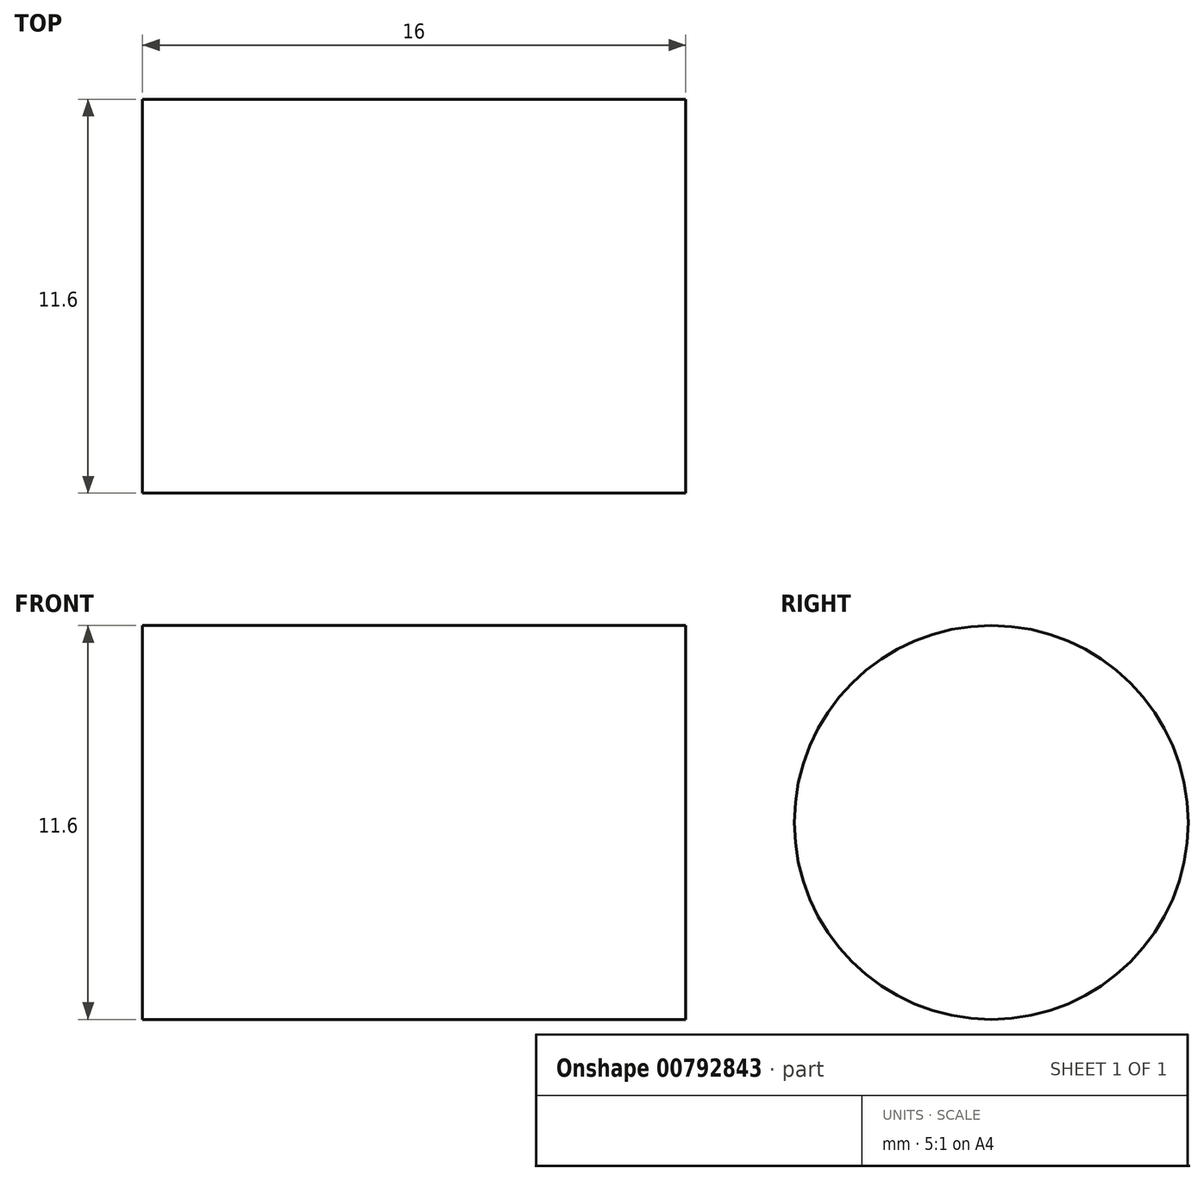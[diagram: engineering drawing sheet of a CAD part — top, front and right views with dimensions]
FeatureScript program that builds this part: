
annotation { "Feature Type Name" : "Feature", "Feature Type Description" : "" }
export const myFeature = defineFeature(function(context is Context, id is Id, definition is map)
    precondition{}
    {
        {
            var Q0;
            Q0=qCreatedBy(makeId("Right.planeOp"), FACE);
            var sketch = newSketch(context, id + "F0", { "sketchPlane" : qUnion([Q0])});
            skCircle(sketch, "E0", {"center": v(0, 0) * mm, "radius": 5.8 * mm});
            skSolve(sketch);
        }
        {
            var Q0;
            Q0 = qSketchRegion(id + "F0", true);
            extrude(context, id + "F1", {"entities" : qUnion([Q0]), "domain" : OperationDomain.MODEL, "flatOperationType" : FlatOperationType.REMOVE, "depth" : 16 * mm, "offsetDistance" : 25 * mm});
        }
    });
